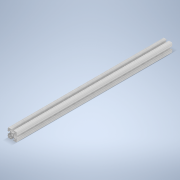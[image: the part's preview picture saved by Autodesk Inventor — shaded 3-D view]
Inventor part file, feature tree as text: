
AUTODESK INVENTOR PART (.ipt)
format: ipt  version: 2020 (Build 240168000, 168)  size: 243,712 bytes
history: native  units: in
note: dims shown in document units (in); Inventor stores cm internally (conversion verified against a paired STEP export)
features: extrude x1, sketch x1, other x1
ambient origin geometry x8: Origin, YZ Plane, XZ Plane, XY Plane, X Axis, Y Axis, Z Axis, Center Point
bodies: Solid1 (feature_tree)
feature tree (3):
  extrude  "Extrusion1"  [1 undecoded]
  sketch  "Sketch1"  dims[d0=10.0in d1=0.0in]
  other  "Boss-Extrude1"
note: 1 required parameter value undecoded (feature->parameter linkage not recoverable at this tier; creation-order binding heuristic only, values carry confidence <= 0.55)
